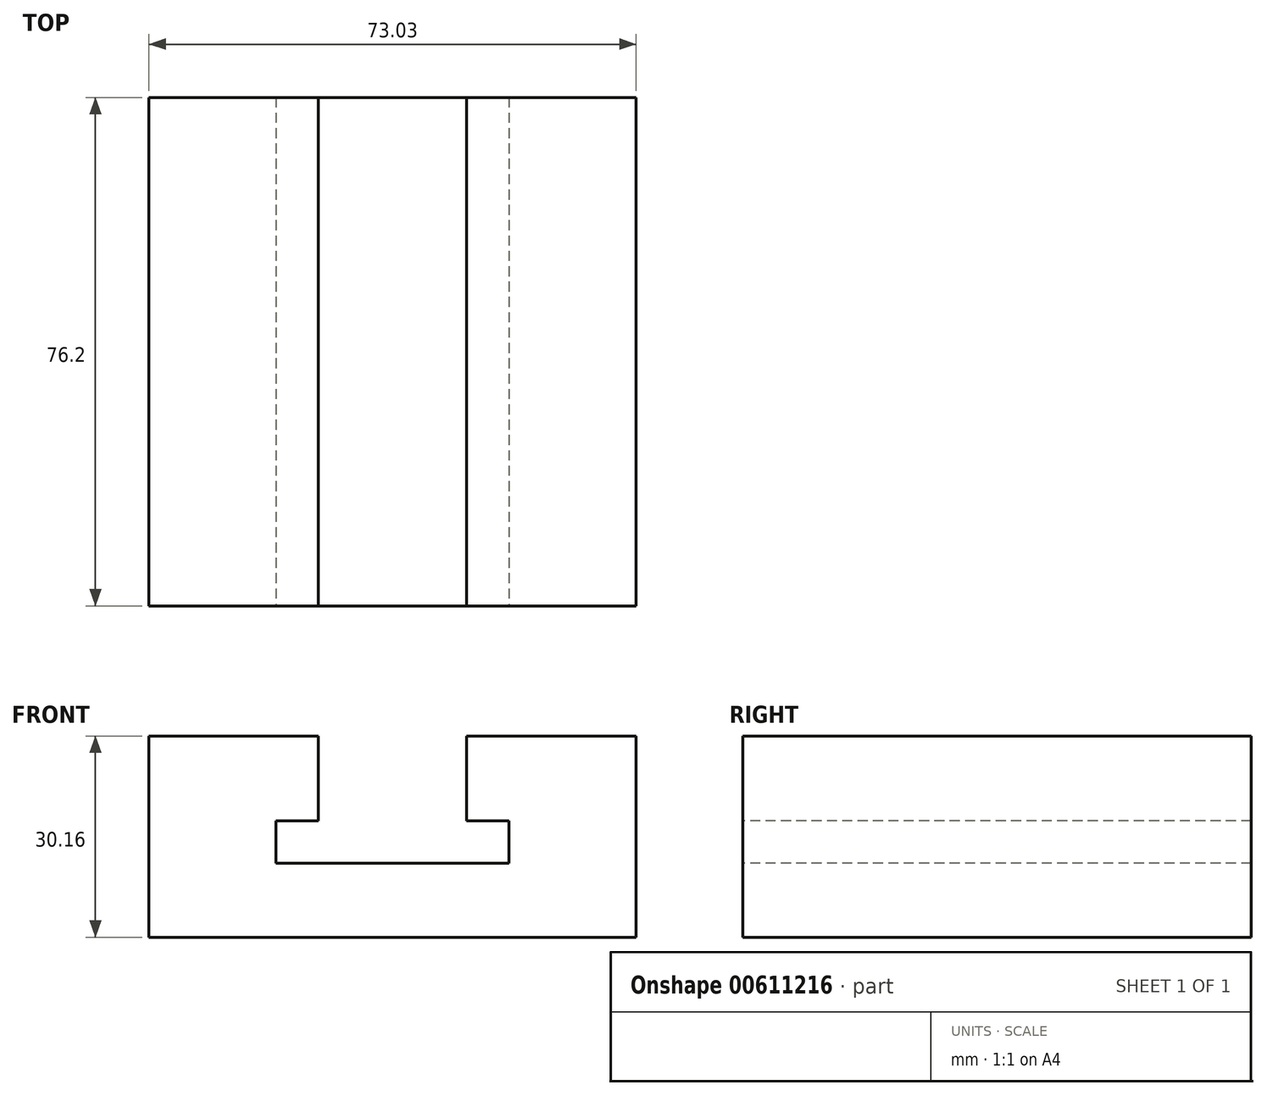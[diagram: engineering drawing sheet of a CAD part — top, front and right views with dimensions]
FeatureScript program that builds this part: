
annotation { "Feature Type Name" : "Feature", "Feature Type Description" : "" }
export const myFeature = defineFeature(function(context is Context, id is Id, definition is map)
    precondition{}
    {
        {
            var Q0;
            Q0=qCreatedBy(makeId("Front.planeOp"),FACE);
            var sketch = newSketch(context, id + "F0", { "sketchPlane" : qUnion([Q0])});
            skLineSegment(sketch, "E0", {"start": v(0, 0) * mm, "end": v(-34.93, 0) * mm});
            skLineSegment(sketch, "E1", {"start": v(-34.93, 0) * mm, "end": v(-34.93, 6.35) * mm});
            skLineSegment(sketch, "E2", {"start": v(-34.93, 6.35) * mm, "end": v(-28.58, 6.35) * mm});
            skLineSegment(sketch, "E3", {"start": v(-28.58, 6.35) * mm, "end": v(-28.58, 19.05) * mm});
            skLineSegment(sketch, "E4", {"start": v(0, 0) * mm, "end": v(0, 6.35) * mm});
            skLineSegment(sketch, "E5", {"start": v(0, 6.35) * mm, "end": v(-6.35, 6.35) * mm});
            skLineSegment(sketch, "E6", {"start": v(-6.35, 6.35) * mm, "end": v(-6.35, 19.05) * mm});
            skLineSegment(sketch, "E7", {"start": v(19.05, 19.05) * mm, "end": v(-6.35, 19.05) * mm});
            skLineSegment(sketch, "E8", {"start": v(19.05, 19.05) * mm, "end": v(19.05, -11.11) * mm});
            skLineSegment(sketch, "E9", {"start": v(19.05, -11.11) * mm, "end": v(-53.98, -11.11) * mm});
            skLineSegment(sketch, "E10", {"start": v(-53.98, 19.05) * mm, "end": v(-28.58, 19.05) * mm});
            skLineSegment(sketch, "E11", {"start": v(-53.98, 19.05) * mm, "end": v(-53.98, -11.11) * mm});
            skSolve(sketch);
        }
        {
            var Q0;
            Q0 = qSketchRegion(id + "F0", true);
            extrude(context, id + "F1", {"entities" : qUnion([Q0]), "oppositeDirection" : true, "depth" : 76.2 * mm, "offsetDistance" : 25.4 * mm});
        }
    });
